# Revit family: ledstreetlight-e2_20w-4000-dd_705000022000
name_source: partatom
category: Leuchten
revit_build: Autodesk Revit 2016 (Build: 20190508_0715(x64)
units: mm (PartAtom-declared; Revit-internal decimal feet)

## family parameters
Basisbauteil = Fläche
Beim Laden mit Abzugskörper schneiden = Nein
Bemaßung runder Anschluss = Durchmesser verwenden
Gemeinsam genutzt = Nein
Lichtquelle = Nein
Raumberechnungspunkt = Nein
Teiletyp = Normal

## types (1)
- LEDStreetlight-E2 20W-4000-DD (1 x LED, 2500 lm)
    Approval mark = CE, ENEC
    Beschreibung = Design streetlight luminaire with optimised optical configuration. Up to 60% energy saving compared to traditional streetlights. Accessories available for many pole types and connections. IP66 and suitable for use on the coastal applications. Now with 42-60mm pole entry.
    CIE Flux Codes = 46 80 98 100 100
    Control Gear = Electronic ballast
    Height = 1070 mm
    Hersteller = OPPLE
    Lamp Light Flux = 2500 lm
    Lamp count = 1
    Lampe = 1 x LED
    Length = 389 mm
    Luminous efficacy = 125 lm/W
    ModVariant = Nein
    Modell = 705000022000
    Mounting Place = Pole
    Mounting Type = Pole top, Pole annexe
    Number of Poles = 1
    OnlyDefault = Ja
    Power Factor = 1
    Product Name = LEDStreetlight-E2 20W-4000-DD
    Product group = Streetlight G2
    ProductGroupID = 6210
    Protection Class = Protection class I
    Protection Degree = IP 66
    RLX_Detail_Level = 1
    RlxData = <blob elided: 204825 chars, md5=0fa93851>
    Scheinlast = 20 VA
    Socket = socket
    Standby Power = 0 W
    System Light Flux = 2500 lm
    System Power = 20 W
    Typenbild = 705000022000.jpg
    Typenkommentare = Product without accessories
    URL = http://relux.com
    VarID = ---
    Voltage = 0 V
    Vorgabe-Ansicht = 1800 mm
    Weight = 0.00 kg
    Width = 140 mm  [stored 0.459318 ft]

note: [stored X ft] marks values corroborated as IEEE doubles in the binary element streams (Revit-internal decimal feet)

## geometry (parser evidence)
native form markers: Sweep x7
no freeform markers — native parametric forms only
